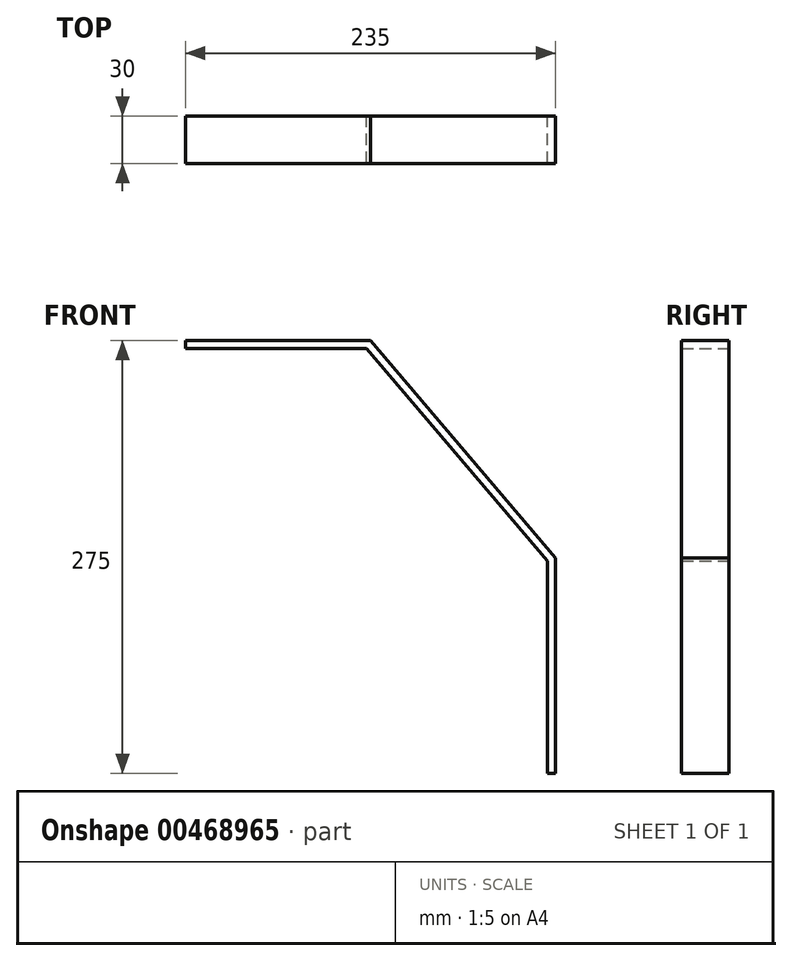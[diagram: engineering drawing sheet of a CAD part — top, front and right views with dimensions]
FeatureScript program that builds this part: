
annotation { "Feature Type Name" : "Feature", "Feature Type Description" : "" }
export const myFeature = defineFeature(function(context is Context, id is Id, definition is map)
    precondition{}
    {
        {
            var Q0;
            Q0=qCreatedBy(makeId("Front.planeOp"),FACE);
            var sketch = newSketch(context, id + "F0", { "sketchPlane" : qUnion([Q0])});
            skLineSegment(sketch, "E0.top", {"start": v(-115, 270) * mm, "end": v(-230, 270) * mm});
            skLineSegment(sketch, "E0.left", {"start": v(0, 0) * mm, "end": v(0, 135) * mm});
            skLineSegment(sketch, "E1", {"start": v(0, 135) * mm, "end": v(-115, 270) * mm});
            skPoint(sketch, "E2.orphan", {"position": v(0, 270) * mm});
            skLineSegment(sketch, "E3.1", {"start": v(-112.7, 275) * mm, "end": v(-230, 275) * mm});
            skLineSegment(sketch, "E3.2", {"start": v(5, 136.84) * mm, "end": v(-112.7, 275) * mm});
            skLineSegment(sketch, "E3.3", {"start": v(5, 0) * mm, "end": v(5, 136.84) * mm});
            skLineSegment(sketch, "E4", {"start": v(-230, 270) * mm, "end": v(-230, 275) * mm});
            skLineSegment(sketch, "E5", {"start": v(0, 0) * mm, "end": v(5, 0) * mm});
            skSolve(sketch);
        }
        {
            var Q0;
            Q0 = qSketchRegion(id + "F0", true);
            extrude(context, id + "F1", {"entities" : qUnion([Q0]), "depth" : 30 * mm});
        }
    });
